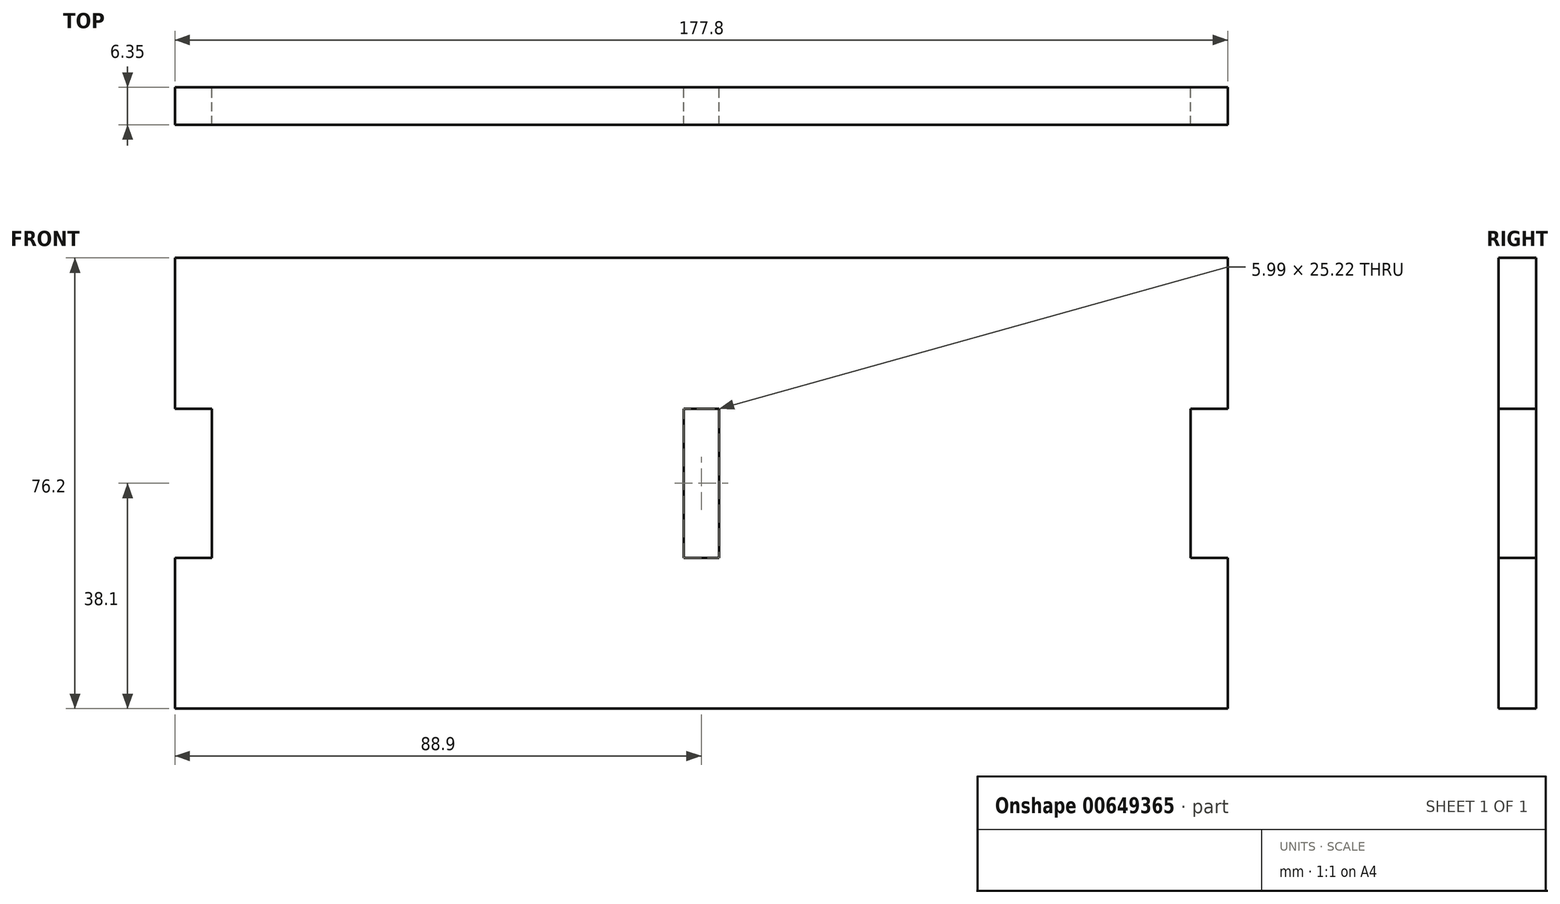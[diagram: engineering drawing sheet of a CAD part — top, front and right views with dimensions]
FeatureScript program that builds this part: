
annotation { "Feature Type Name" : "Feature", "Feature Type Description" : "" }
export const myFeature = defineFeature(function(context is Context, id is Id, definition is map)
    precondition{}
    {
        {
            var Q0;
            Q0=qCreatedBy(makeId("Front.planeOp"),FACE);
            var sketch = newSketch(context, id + "F0", { "sketchPlane" : qUnion([Q0])});
            skLineSegment(sketch, "E0.bottom", {"start": v(0, 0) * mm, "end": v(177.8, 0) * mm});
            skLineSegment(sketch, "E0.top", {"start": v(0, 76.2) * mm, "end": v(177.8, 76.2) * mm});
            skLineSegment(sketch, "E0.left", {"start": v(0, 0) * mm, "end": v(0, 76.2) * mm});
            skLineSegment(sketch, "E0.right", {"start": v(177.8, 0) * mm, "end": v(177.8, 76.2) * mm});
            skLineSegment(sketch, "E1.bottom", {"start": v(25.31, 0) * mm, "end": v(50.89, 0) * mm});
            skLineSegment(sketch, "E1.top", {"start": v(25.15, -6.44) * mm, "end": v(50.73, -6.44) * mm});
            skLineSegment(sketch, "E1.left", {"start": v(25.31, 0) * mm, "end": v(25.15, -6.44) * mm});
            skLineSegment(sketch, "E1.right", {"start": v(50.89, 0) * mm, "end": v(50.73, -6.44) * mm});
            skLineSegment(sketch, "E2.bottom", {"start": v(76.11, 0) * mm, "end": v(101.69, 0) * mm});
            skLineSegment(sketch, "E2.top", {"start": v(76.11, -6.44) * mm, "end": v(101.69, -6.44) * mm});
            skLineSegment(sketch, "E2.left", {"start": v(76.11, 0) * mm, "end": v(76.11, -6.44) * mm});
            skLineSegment(sketch, "E2.right", {"start": v(101.69, 0) * mm, "end": v(101.69, -6.44) * mm});
            skLineSegment(sketch, "E3.bottom", {"start": v(126.91, 0) * mm, "end": v(152.49, 0) * mm});
            skLineSegment(sketch, "E3.top", {"start": v(126.91, -6.44) * mm, "end": v(152.49, -6.44) * mm});
            skLineSegment(sketch, "E3.left", {"start": v(126.91, 0) * mm, "end": v(126.91, -6.44) * mm});
            skLineSegment(sketch, "E3.right", {"start": v(152.49, 0) * mm, "end": v(152.49, -6.44) * mm});
            skPoint(sketch, "E4", {"position": v(38.1, 0) * mm});
            skPoint(sketch, "E5", {"position": v(88.9, 0) * mm});
            skPoint(sketch, "E6", {"position": v(139.7, 0) * mm});
            skLineSegment(sketch, "E7.bottom", {"start": v(0, 50.71) * mm, "end": v(6.26, 50.71) * mm});
            skLineSegment(sketch, "E7.top", {"start": v(0, 25.49) * mm, "end": v(6.26, 25.49) * mm});
            skLineSegment(sketch, "E7.left", {"start": v(0, 38.1) * mm, "end": v(0, 25.49) * mm});
            skLineSegment(sketch, "E7.right", {"start": v(6.26, 50.71) * mm, "end": v(6.26, 25.49) * mm});
            skLineSegment(sketch, "E8.bottom", {"start": v(177.8, 50.71) * mm, "end": v(171.54, 50.71) * mm});
            skLineSegment(sketch, "E8.top", {"start": v(177.8, 25.49) * mm, "end": v(171.54, 25.49) * mm});
            skLineSegment(sketch, "E8.left", {"start": v(177.8, 50.71) * mm, "end": v(177.8, 25.49) * mm});
            skLineSegment(sketch, "E8.right", {"start": v(171.54, 50.71) * mm, "end": v(171.54, 25.49) * mm});
            skPoint(sketch, "E9", {"position": v(0, 38.1) * mm});
            skPoint(sketch, "E10", {"position": v(177.8, 38.1) * mm});
            skLineSegment(sketch, "E11.bottom", {"start": v(85.9, 50.71) * mm, "end": v(91.9, 50.71) * mm});
            skLineSegment(sketch, "E11.top", {"start": v(85.9, 25.49) * mm, "end": v(91.9, 25.49) * mm});
            skLineSegment(sketch, "E11.left", {"start": v(85.9, 50.71) * mm, "end": v(85.9, 25.49) * mm});
            skLineSegment(sketch, "E11.right", {"start": v(91.9, 50.71) * mm, "end": v(91.9, 25.49) * mm});
            skPoint(sketch, "E12", {"position": v(88.9, 50.71) * mm});
            skLineSegment(sketch, "E13", {"start": v(0, 38.1) * mm, "end": v(177.8, 38.1) * mm, "construction": true});
            skSolve(sketch);
        }
        {
            var Q0;
            {var subQ2=sQuery(id+"F0.wireOp",EDGE,"E0.top");Q0=makeQuery(id+"F0.imprint","IMPRINT",FACE,{"disambiguationData":[TD([[makeQuery(id+"F0.imprint","IMPRINT",EDGE,{"derivedFrom":subQ2}),-1.0]])]});}
            var Q1;
            Q1=makeQuery(id+"F0.imprint","IMPRINT",FACE,{"disambiguationData":[TD([[makeQuery(id+"F0.imprint","IMPRINT",EDGE,{"derivedFrom":sQuery(id+"F0.wireOp",EDGE,"E1.bottom")}),-1.0]])]});
            var Q2;
            Q2=makeQuery(id+"F0.imprint","IMPRINT",FACE,{"disambiguationData":[TD([[makeQuery(id+"F0.imprint","IMPRINT",EDGE,{"derivedFrom":sQuery(id+"F0.wireOp",EDGE,"E2.bottom")}),-1.0]])]});
            var Q3;
            Q3=makeQuery(id+"F0.imprint","IMPRINT",FACE,{"disambiguationData":[TD([[makeQuery(id+"F0.imprint","IMPRINT",EDGE,{"derivedFrom":sQuery(id+"F0.wireOp",EDGE,"E3.bottom")}),-1.0]])]});
            extrude(context, id + "F1", {"entities" : qUnion([Q0, Q1, Q2, Q3]), "depth" : 6.35 * mm, "offsetDistance" : 25.4 * mm});
        }
    });
